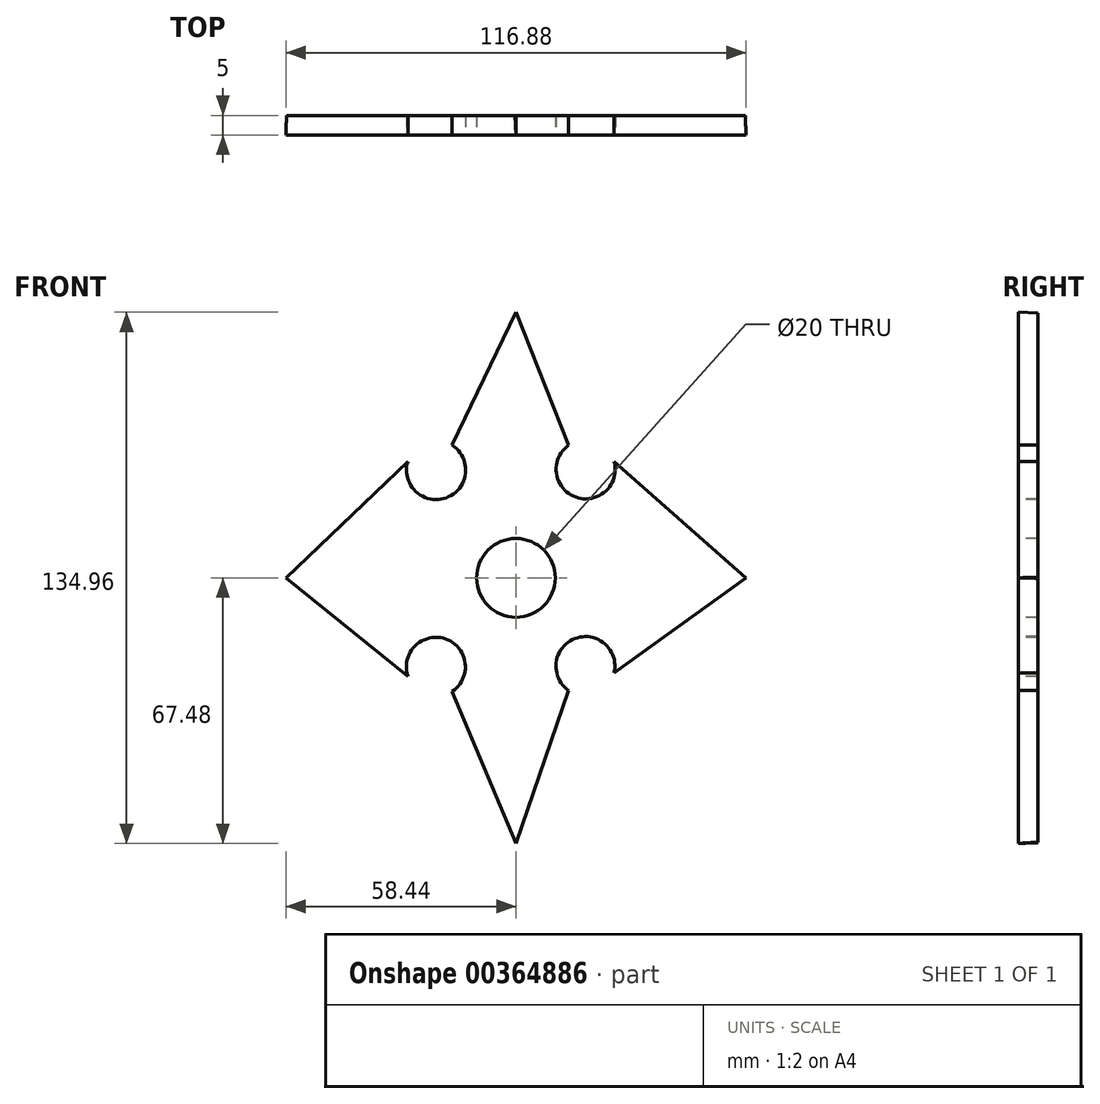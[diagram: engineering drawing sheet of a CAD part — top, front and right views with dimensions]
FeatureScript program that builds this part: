
annotation { "Feature Type Name" : "Feature", "Feature Type Description" : "" }
export const myFeature = defineFeature(function(context is Context, id is Id, definition is map)
    precondition{}
    {
        {
            var Q0;
            Q0=qCreatedBy(makeId("Front.planeOp"),FACE);
            var sketch = newSketch(context, id + "F0", { "sketchPlane" : qUnion([Q0])});
            skCircle(sketch, "E0.cCircle", {"center": v(0, 0) * mm, "radius": 58.29 * mm, "construction": true});
            skLineSegment(sketch, "E0.0", {"start": v(-58.24, 33.73) * mm, "end": v(0.09, 67.3) * mm});
            skLineSegment(sketch, "E0.1", {"start": v(0.09, 67.3) * mm, "end": v(58.33, 33.57) * mm});
            skLineSegment(sketch, "E0.2", {"start": v(58.33, 33.57) * mm, "end": v(58.24, -33.73) * mm});
            skLineSegment(sketch, "E0.3", {"start": v(58.24, -33.73) * mm, "end": v(-0.09, -67.3) * mm});
            skLineSegment(sketch, "E0.4", {"start": v(-0.09, -67.3) * mm, "end": v(-58.33, -33.57) * mm});
            skLineSegment(sketch, "E0.5", {"start": v(-58.33, -33.57) * mm, "end": v(-58.24, 33.73) * mm});
            skPoint(sketch, "E0.0.midPoint", {"position": v(-29.08, 50.52) * mm});
            skSolve(sketch);
        }
        {
            var Q0;
            Q0=qCreatedBy(makeId("Front.planeOp"),FACE);
            cPlane(context, id + "F1", {"entities" : qUnion([Q0]), "cplaneType" : CPlaneType.OFFSET, "offset" : 5 * mm, "width" : 150 * mm, "height" : 150 * mm});
        }
        {
            var Q0;
            Q0=qCreatedBy(id+"F1.planeOp",FACE);
            var sketch = newSketch(context, id + "F2", { "sketchPlane" : qUnion([Q0])});
            skCircle(sketch, "E1.cCircle", {"center": v(0, 0) * mm, "radius": 58.44 * mm, "construction": true});
            skLineSegment(sketch, "E1.0", {"start": v(-58.46, 33.7) * mm, "end": v(-0.05, 67.48) * mm});
            skLineSegment(sketch, "E1.1", {"start": v(-0.05, 67.48) * mm, "end": v(58.41, 33.78) * mm});
            skLineSegment(sketch, "E1.2", {"start": v(58.41, 33.78) * mm, "end": v(58.46, -33.7) * mm});
            skLineSegment(sketch, "E1.3", {"start": v(58.46, -33.7) * mm, "end": v(0.05, -67.48) * mm});
            skLineSegment(sketch, "E1.4", {"start": v(0.05, -67.48) * mm, "end": v(-58.41, -33.78) * mm});
            skLineSegment(sketch, "E1.5", {"start": v(-58.41, -33.78) * mm, "end": v(-58.46, 33.7) * mm});
            skPoint(sketch, "E1.0.midPoint", {"position": v(-29.25, 50.59) * mm});
            skSolve(sketch);
        }
        {
            var Q0;
            Q0=makeQuery(id+"F2.imprint","IMPRINT",FACE,{"disambiguationData":[TD([[makeQuery(id+"F2.imprint","IMPRINT",EDGE,{"derivedFrom":sQuery(id+"F2.wireOp",EDGE,"E1.0")}),-1.0]])]});
            var Q1;
            Q1=makeQuery(id+"F0.imprint","IMPRINT",FACE,{"disambiguationData":[TD([[makeQuery(id+"F0.imprint","IMPRINT",EDGE,{"derivedFrom":sQuery(id+"F0.wireOp",EDGE,"E0.0")}),-1.0]])]});
            loft(context, id + "F3", {"sheetProfilesArray" : [{ "sheetProfileEntities" : qUnion([Q0]) }, { "sheetProfileEntities" : qUnion([Q1]) }]});
        }
        {
            var Q0;
            Q0=makeQuery(id+"F3.opLoft","CAP_FACE",FACE,{"disambiguationData":[OSD([makeQuery(id+"F2.imprint","IMPRINT",FACE,{"disambiguationData":[TD([[makeQuery(id+"F2.imprint","IMPRINT",EDGE,{"derivedFrom":sQuery(id+"F2.wireOp",EDGE,"E1.0")}),-1.0]])]})])],"isStart":true});
            var sketch = newSketch(context, id + "F4", { "sketchPlane" : qUnion([Q0])});
            skCircle(sketch, "E2", {"center": v(0, 0) * mm, "radius": 10 * mm});
            skSolve(sketch);
        }
        {
            var Q0;
            Q0=makeQuery(id+"F4.imprint","IMPRINT",FACE,{"disambiguationData":[TD([[makeQuery(id+"F4.imprint","IMPRINT",EDGE,{"derivedFrom":sQuery(id+"F4.wireOp",EDGE,"E2")}),1.0]])]});
            extrude(context, id + "F5", {"entities" : qUnion([Q0]), "operationType" : NewBodyOperationType.REMOVE, "oppositeDirection" : true, "depth" : 25 * mm});
        }
        {
            var Q0;
            Q0=qCreatedBy(id+"F1.planeOp",FACE);
            var sketch = newSketch(context, id + "F6", { "sketchPlane" : qUnion([Q0])});
            skCircle(sketch, "E3", {"center": v(-20.28, 27.4) * mm, "radius": 7.5 * mm});
            skPoint(sketch, "E3.first.point", {"position": v(-18.43, 20.12) * mm});
            skPoint(sketch, "E3.second.point", {"position": v(-22.55, 34.54) * mm});
            skPoint(sketch, "E3.third.point", {"position": v(-27.7, 26.3) * mm});
            skCircle(sketch, "E4", {"center": v(17.72, 27.57) * mm, "radius": 7.5 * mm});
            skPoint(sketch, "E4.first.point", {"position": v(14.42, 20.84) * mm});
            skPoint(sketch, "E4.second.point", {"position": v(11.69, 32.02) * mm});
            skPoint(sketch, "E4.third.point", {"position": v(25.15, 26.54) * mm});
            skCircle(sketch, "E5", {"center": v(-20.34, -22.6) * mm, "radius": 7.5 * mm});
            skPoint(sketch, "E5.first.point", {"position": v(-15.33, -28.19) * mm});
            skPoint(sketch, "E5.second.point", {"position": v(-27.83, -22.96) * mm});
            skPoint(sketch, "E5.third.point", {"position": v(-23.16, -15.66) * mm});
            skCircle(sketch, "E6", {"center": v(17.66, -22.43) * mm, "radius": 7.5 * mm});
            skPoint(sketch, "E6.first.point", {"position": v(17.72, -29.93) * mm});
            skPoint(sketch, "E6.second.point", {"position": v(14.42, -15.66) * mm});
            skPoint(sketch, "E6.third.point", {"position": v(25.15, -22.11) * mm});
            skSolve(sketch);
        }
        {
            var Q0;
            Q0=makeQuery(id+"F6.imprint","IMPRINT",FACE,{"disambiguationData":[TD([[makeQuery(id+"F6.imprint","IMPRINT",EDGE,{"derivedFrom":sQuery(id+"F6.wireOp",EDGE,"E3")}),1.0]])]});
            var Q1;
            Q1=makeQuery(id+"F6.imprint","IMPRINT",FACE,{"disambiguationData":[TD([[makeQuery(id+"F6.imprint","IMPRINT",EDGE,{"derivedFrom":sQuery(id+"F6.wireOp",EDGE,"E4")}),1.0]])]});
            var Q2;
            Q2=makeQuery(id+"F6.imprint","IMPRINT",FACE,{"disambiguationData":[TD([[makeQuery(id+"F6.imprint","IMPRINT",EDGE,{"derivedFrom":sQuery(id+"F6.wireOp",EDGE,"E5")}),1.0]])]});
            var Q3;
            Q3=makeQuery(id+"F6.imprint","IMPRINT",FACE,{"disambiguationData":[TD([[makeQuery(id+"F6.imprint","IMPRINT",EDGE,{"derivedFrom":sQuery(id+"F6.wireOp",EDGE,"E6")}),1.0]])]});
            extrude(context, id + "F7", {"entities" : qUnion([Q0, Q1, Q2, Q3]), "operationType" : NewBodyOperationType.REMOVE, "oppositeDirection" : true, "depth" : 25 * mm});
        }
        {
            var Q0;
            Q0=makeQuery(id+"F3.opLoft","CAP_FACE",FACE,{"disambiguationData":[OSD([makeQuery(id+"F2.imprint","IMPRINT",FACE,{"disambiguationData":[TD([[makeQuery(id+"F2.imprint","IMPRINT",EDGE,{"derivedFrom":sQuery(id+"F2.wireOp",EDGE,"E1.0")}),-1.0]])]})])],"isStart":true});
            var sketch = newSketch(context, id + "F8", { "sketchPlane" : qUnion([Q0])});
            skFitSpline(sketch, "E7", {"points": [v(-58.46, 33.7) * mm, v(-27.45, 29.57) * mm], "startDerivative": vector(31.01, -4.13) * mm, "endDerivative": vector(31.01, -4.13) * mm});
            skFitSpline(sketch, "E8", {"points": [v(-0.05, 67.48) * mm, v(-16.22, 33.7) * mm], "startDerivative": vector(-16.17, -33.78) * mm, "endDerivative": vector(-16.17, -33.78) * mm});
            skFitSpline(sketch, "E9", {"points": [v(-58.46, 33.7) * mm, v(-0.05, 67.48) * mm], "startDerivative": vector(58.41, 33.78) * mm, "endDerivative": vector(58.41, 33.78) * mm});
            skSolve(sketch);
        }
        {
            var Q0;
            {var subQ0=sQuery(id+"F8.wireOp",EDGE,"E7");Q0=makeQuery(id+"F8.imprint","IMPRINT",FACE,{"disambiguationData":[TD([[makeQuery(id+"F8.imprint","IMPRINT",EDGE,{"derivedFrom":subQ0}),1.0]])]});}
            extrude(context, id + "F9", {"entities" : qUnion([Q0]), "operationType" : NewBodyOperationType.REMOVE, "oppositeDirection" : true, "depth" : 25 * mm});
        }
        {
            var Q0;
            Q0=makeQuery(id+"F3.opLoft","CAP_FACE",FACE,{"disambiguationData":[OSD([makeQuery(id+"F2.imprint","IMPRINT",FACE,{"disambiguationData":[TD([[makeQuery(id+"F2.imprint","IMPRINT",EDGE,{"derivedFrom":sQuery(id+"F2.wireOp",EDGE,"E1.0")}),-1.0]])]})])],"isStart":true});
            var sketch = newSketch(context, id + "F10", { "sketchPlane" : qUnion([Q0])});
            skFitSpline(sketch, "E10", {"points": [v(-0.05, 67.48) * mm, v(13.4, 33.7) * mm], "startDerivative": vector(13.44, -33.78) * mm, "endDerivative": vector(13.44, -33.78) * mm});
            skFitSpline(sketch, "E11", {"points": [v(58.41, 33.78) * mm, v(24.95, 29.57) * mm], "startDerivative": vector(-33.46, -4.21) * mm, "endDerivative": vector(-33.46, -4.21) * mm});
            skFitSpline(sketch, "E12", {"points": [v(58.46, -33.7) * mm, v(24.95, -24.17) * mm], "startDerivative": vector(-33.5, 9.52) * mm, "endDerivative": vector(-33.5, 9.52) * mm});
            skFitSpline(sketch, "E13", {"points": [v(0.05, -67.48) * mm, v(13.4, -28.6) * mm], "startDerivative": vector(13.34, 38.88) * mm, "endDerivative": vector(13.34, 38.88) * mm});
            skFitSpline(sketch, "E14", {"points": [v(0.05, -67.48) * mm, v(-16.22, -28.87) * mm], "startDerivative": vector(-16.26, 38.6) * mm, "endDerivative": vector(-16.26, 38.6) * mm});
            skFitSpline(sketch, "E15", {"points": [v(-58.41, -33.78) * mm, v(-27.45, -24.99) * mm], "startDerivative": vector(30.96, 8.8) * mm, "endDerivative": vector(30.96, 8.8) * mm});
            skSolve(sketch);
        }
        {
            var Q0;
            {var subQ0=sQuery(id+"F10.wireOp",EDGE,"E14");Q0=makeQuery(id+"F10.imprint","IMPRINT",FACE,{"disambiguationData":[TD([[makeQuery(id+"F10.imprint","IMPRINT",EDGE,{"derivedFrom":subQ0}),1.0]])]});}
            var Q1;
            {var subQ0=sQuery(id+"F10.wireOp",EDGE,"E12");Q1=makeQuery(id+"F10.imprint","IMPRINT",FACE,{"disambiguationData":[TD([[makeQuery(id+"F10.imprint","IMPRINT",EDGE,{"derivedFrom":subQ0}),1.0]])]});}
            var Q2;
            {var subQ0=sQuery(id+"F10.wireOp",EDGE,"E10");Q2=makeQuery(id+"F10.imprint","IMPRINT",FACE,{"disambiguationData":[TD([[makeQuery(id+"F10.imprint","IMPRINT",EDGE,{"derivedFrom":subQ0}),1.0]])]});}
            extrude(context, id + "F11", {"entities" : qUnion([Q0, Q1, Q2]), "operationType" : NewBodyOperationType.REMOVE, "oppositeDirection" : true, "depth" : 25 * mm});
        }
        {
            var Q0;
            Q0=makeQuery(id+"F3.opLoft","CAP_FACE",FACE,{"disambiguationData":[OSD([makeQuery(id+"F2.imprint","IMPRINT",FACE,{"disambiguationData":[TD([[makeQuery(id+"F2.imprint","IMPRINT",EDGE,{"derivedFrom":sQuery(id+"F2.wireOp",EDGE,"E1.0")}),-1.0]])]})])],"isStart":true});
            var sketch = newSketch(context, id + "F12", { "sketchPlane" : qUnion([Q0])});
            skFitSpline(sketch, "E16", {"points": [v(58.44, 0) * mm, v(24.95, 29.57) * mm], "startDerivative": vector(-33.48, 29.57) * mm, "endDerivative": vector(-33.48, 29.57) * mm});
            skFitSpline(sketch, "E17", {"points": [v(24.95, 29.57) * mm, v(58.41, 33.78) * mm], "startDerivative": vector(33.46, 4.21) * mm, "endDerivative": vector(33.46, 4.21) * mm});
            skFitSpline(sketch, "E18", {"points": [v(58.41, 33.78) * mm, v(58.44, 0) * mm], "startDerivative": vector(0.02, -33.78) * mm, "endDerivative": vector(0.02, -33.78) * mm});
            skFitSpline(sketch, "E19", {"points": [v(58.44, 0) * mm, v(24.95, -24.17) * mm], "startDerivative": vector(-33.48, -24.17) * mm, "endDerivative": vector(-33.48, -24.17) * mm});
            skFitSpline(sketch, "E20", {"points": [v(58.46, -33.7) * mm, v(58.44, 0) * mm], "startDerivative": vector(-0.02, 33.7) * mm, "endDerivative": vector(-0.02, 33.7) * mm});
            skSolve(sketch);
        }
        {
            var Q0;
            Q0=makeQuery(id+"F12.imprint","IMPRINT",FACE,{"disambiguationData":[TD([[makeQuery(id+"F12.imprint","IMPRINT",EDGE,{"derivedFrom":sQuery(id+"F12.wireOp",EDGE,"E19")}),1.0]])]});
            var Q1;
            Q1=makeQuery(id+"F12.imprint","IMPRINT",FACE,{"disambiguationData":[TD([[makeQuery(id+"F12.imprint","IMPRINT",EDGE,{"derivedFrom":sQuery(id+"F12.wireOp",EDGE,"E16")}),-1.0]])]});
            extrude(context, id + "F13", {"entities" : qUnion([Q0, Q1]), "operationType" : NewBodyOperationType.REMOVE, "oppositeDirection" : true, "depth" : 25 * mm});
        }
        {
            var Q0;
            Q0=makeQuery(id+"F3.opLoft","CAP_FACE",FACE,{"disambiguationData":[OSD([makeQuery(id+"F2.imprint","IMPRINT",FACE,{"disambiguationData":[TD([[makeQuery(id+"F2.imprint","IMPRINT",EDGE,{"derivedFrom":sQuery(id+"F2.wireOp",EDGE,"E1.0")}),-1.0]])]})])],"isStart":true});
            var sketch = newSketch(context, id + "F14", { "sketchPlane" : qUnion([Q0])});
            skPoint(sketch, "E21.1.internal.orphan", {"position": v(-58.44, -0.04) * mm});
            skFitSpline(sketch, "E22", {"points": [v(-27.45, 29.57) * mm, v(-58.44, -0.04) * mm], "startDerivative": vector(-30.98, -29.6) * mm, "endDerivative": vector(-30.98, -29.6) * mm});
            skFitSpline(sketch, "E23", {"points": [v(-58.44, -0.04) * mm, v(-27.45, -24.99) * mm], "startDerivative": vector(30.98, -24.95) * mm, "endDerivative": vector(30.98, -24.95) * mm});
            skFitSpline(sketch, "E24", {"points": [v(-58.44, -0.04) * mm, v(-58.41, -33.78) * mm], "startDerivative": vector(0.02, -33.74) * mm, "endDerivative": vector(0.02, -33.74) * mm});
            skFitSpline(sketch, "E25", {"points": [v(-58.41, -33.78) * mm, v(-27.45, -24.99) * mm], "startDerivative": vector(30.96, 8.8) * mm, "endDerivative": vector(30.96, 8.8) * mm});
            skFitSpline(sketch, "E26", {"points": [v(-58.44, -0.04) * mm, v(-58.46, 33.7) * mm], "startDerivative": vector(-0.02, 33.74) * mm, "endDerivative": vector(-0.02, 33.74) * mm});
            skFitSpline(sketch, "E27", {"points": [v(-58.46, 33.7) * mm, v(-27.45, 29.57) * mm], "startDerivative": vector(31, -4.13) * mm, "endDerivative": vector(31, -4.13) * mm});
            skSolve(sketch);
        }
        {
            var Q0;
            {var subQ0=sQuery(id+"F14.wireOp",EDGE,"E22");Q0=makeQuery(id+"F14.imprint","IMPRINT",FACE,{"disambiguationData":[TD([[makeQuery(id+"F14.imprint","IMPRINT",EDGE,{"derivedFrom":subQ0}),-1.0]])]});}
            var Q1;
            Q1=makeQuery(id+"F14.imprint","IMPRINT",FACE,{"disambiguationData":[TD([[makeQuery(id+"F14.imprint","IMPRINT",EDGE,{"derivedFrom":sQuery(id+"F14.wireOp",EDGE,"E23")}),-1.0]])]});
            extrude(context, id + "F15", {"entities" : qUnion([Q0, Q1]), "operationType" : NewBodyOperationType.REMOVE, "oppositeDirection" : true, "depth" : 25 * mm});
        }
    });
